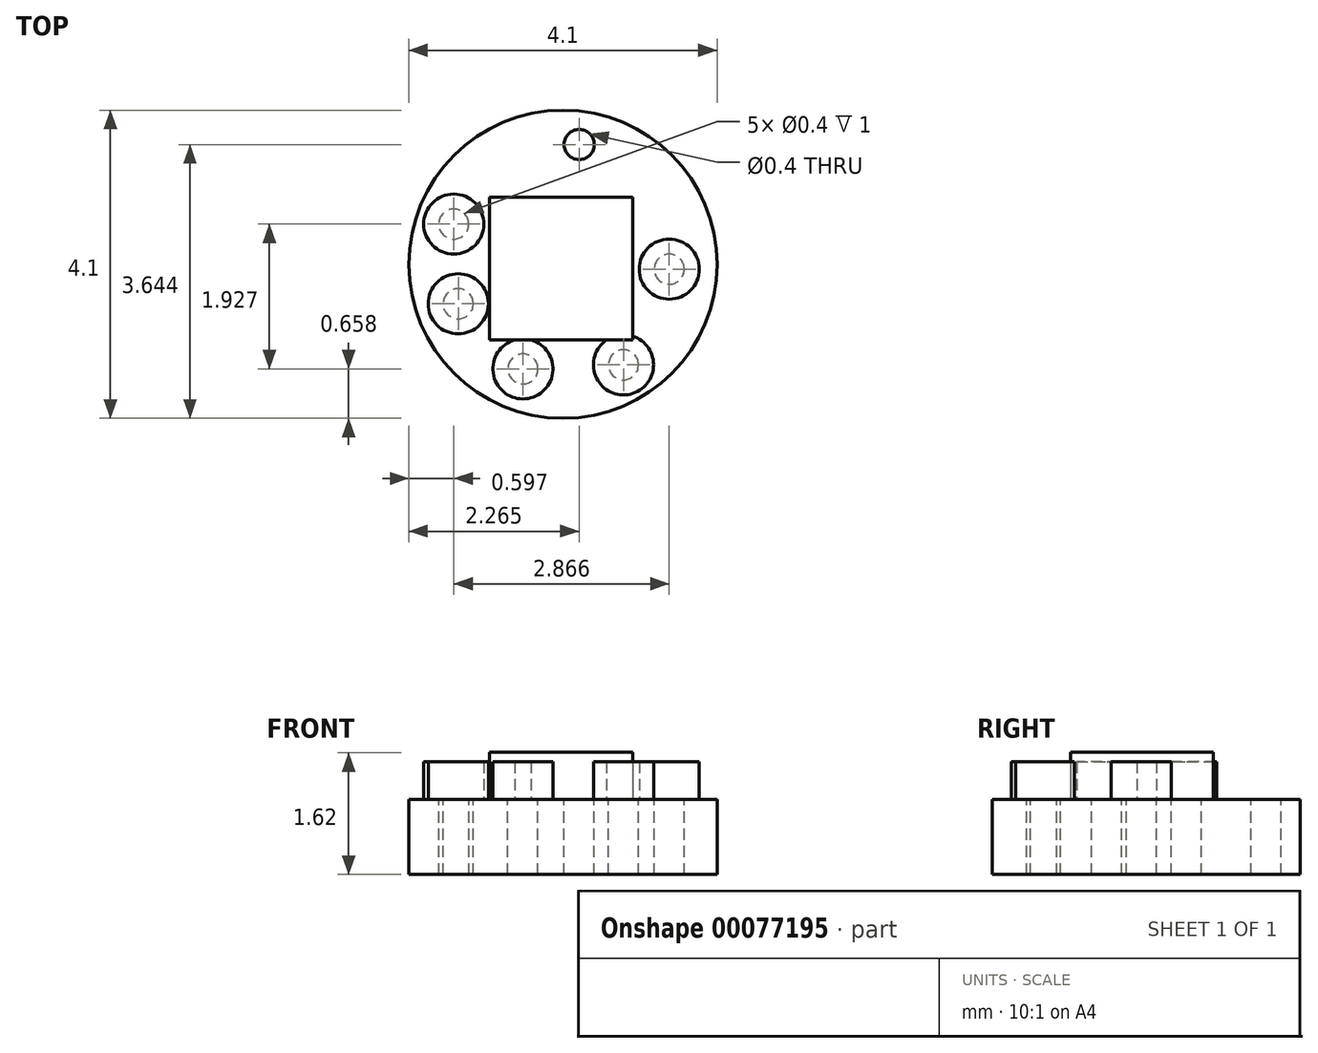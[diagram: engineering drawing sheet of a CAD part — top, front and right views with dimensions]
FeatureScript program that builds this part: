
annotation { "Feature Type Name" : "Feature", "Feature Type Description" : "" }
export const myFeature = defineFeature(function(context is Context, id is Id, definition is map)
    precondition{}
    {
        {
            var Q0;
            Q0=qCreatedBy(makeId("Top.planeOp"),FACE);
            var sketch = newSketch(context, id + "F0", { "sketchPlane" : qUnion([Q0])});
            skCircle(sketch, "E0", {"center": v(0, 0) * mm, "radius": 2.05 * mm});
            skSolve(sketch);
        }
        {
            var Q0;
            Q0=qSketchRegion(id+"F0",true);
            extrude(context, id + "F1", {"entities" : qUnion([Q0]), "depth" : 1 * mm});
        }
        {
            var Q0;
            Q0=makeQuery(id+"F1.opExtrude","CAP_FACE",FACE,{"disambiguationData":[OSD([sQuery(id+"F0.wireOp",EDGE,"E0")])],"isStart":false});
            var sketch = newSketch(context, id + "F2", { "sketchPlane" : qUnion([Q0])});
            skLineSegment(sketch, "E1.bottom", {"start": v(-0.98, 0.9) * mm, "end": v(0.92, 0.9) * mm});
            skLineSegment(sketch, "E1.top", {"start": v(-0.98, -1) * mm, "end": v(0.92, -1) * mm});
            skLineSegment(sketch, "E1.left", {"start": v(-0.98, 0.9) * mm, "end": v(-0.98, -1) * mm});
            skLineSegment(sketch, "E1.right", {"start": v(0.92, 0.9) * mm, "end": v(0.92, -1) * mm});
            skSolve(sketch);
        }
        {
            var Q0;
            Q0=qSketchRegion(id+"F2",true);
            extrude(context, id + "F3", {"entities" : qUnion([Q0]), "depth" : .625 * mm});
        }
        {
            var Q0;
            Q0=makeQuery(id+"F1.opExtrude","CAP_FACE",FACE,{"disambiguationData":[OSD([sQuery(id+"F0.wireOp",EDGE,"E0")])],"isStart":false});
            var sketch = newSketch(context, id + "F4", { "sketchPlane" : qUnion([Q0])});
            skCircle(sketch, "E2", {"center": v(-1.4, -0.53) * mm, "radius": 0.2 * mm});
            skCircle(sketch, "E3", {"center": v(-1.45, 0.54) * mm, "radius": 0.2 * mm});
            skCircle(sketch, "E4", {"center": v(1.41, -0.06) * mm, "radius": 0.2 * mm});
            skCircle(sketch, "E5", {"center": v(0.8, -1.34) * mm, "radius": 0.2 * mm});
            skCircle(sketch, "E6", {"center": v(-0.53, -1.4) * mm, "radius": 0.2 * mm});
            skCircle(sketch, "E7", {"center": v(0.22, 1.6) * mm, "radius": 0.2 * mm});
            skSolve(sketch);
        }
        {
            var Q0;
            Q0=qSketchRegion(id+"F4",true);
            extrude(context, id + "F5", {"entities" : qUnion([Q0]), "operationType" : NewBodyOperationType.REMOVE, "endBound" : BoundingType.THROUGH_ALL, "oppositeDirection" : true, "depth" : 25 * mm});
        }
        {
            var Q0;
            Q0=makeQuery(id+"F1.opExtrude","CAP_FACE",FACE,{"disambiguationData":[OSD([sQuery(id+"F0.wireOp",EDGE,"E0")])],"isStart":false});
            var sketch = newSketch(context, id + "F6", { "sketchPlane" : qUnion([Q0])});
            skCircle(sketch, "E8", {"center": v(-1.4, -0.53) * mm, "radius": 0.4 * mm});
            skCircle(sketch, "E9", {"center": v(-1.45, 0.54) * mm, "radius": 0.4 * mm});
            skCircle(sketch, "E10", {"center": v(1.41, -0.06) * mm, "radius": 0.4 * mm});
            skCircle(sketch, "E11", {"center": v(0.8, -1.34) * mm, "radius": 0.4 * mm});
            skCircle(sketch, "E12", {"center": v(-0.53, -1.4) * mm, "radius": 0.4 * mm});
            skSolve(sketch);
        }
        {
            var Q0;
            Q0=qSketchRegion(id+"F6",true);
            extrude(context, id + "F7", {"entities" : qUnion([Q0]), "operationType" : NewBodyOperationType.ADD, "depth" : .5 * mm});
        }
    });
